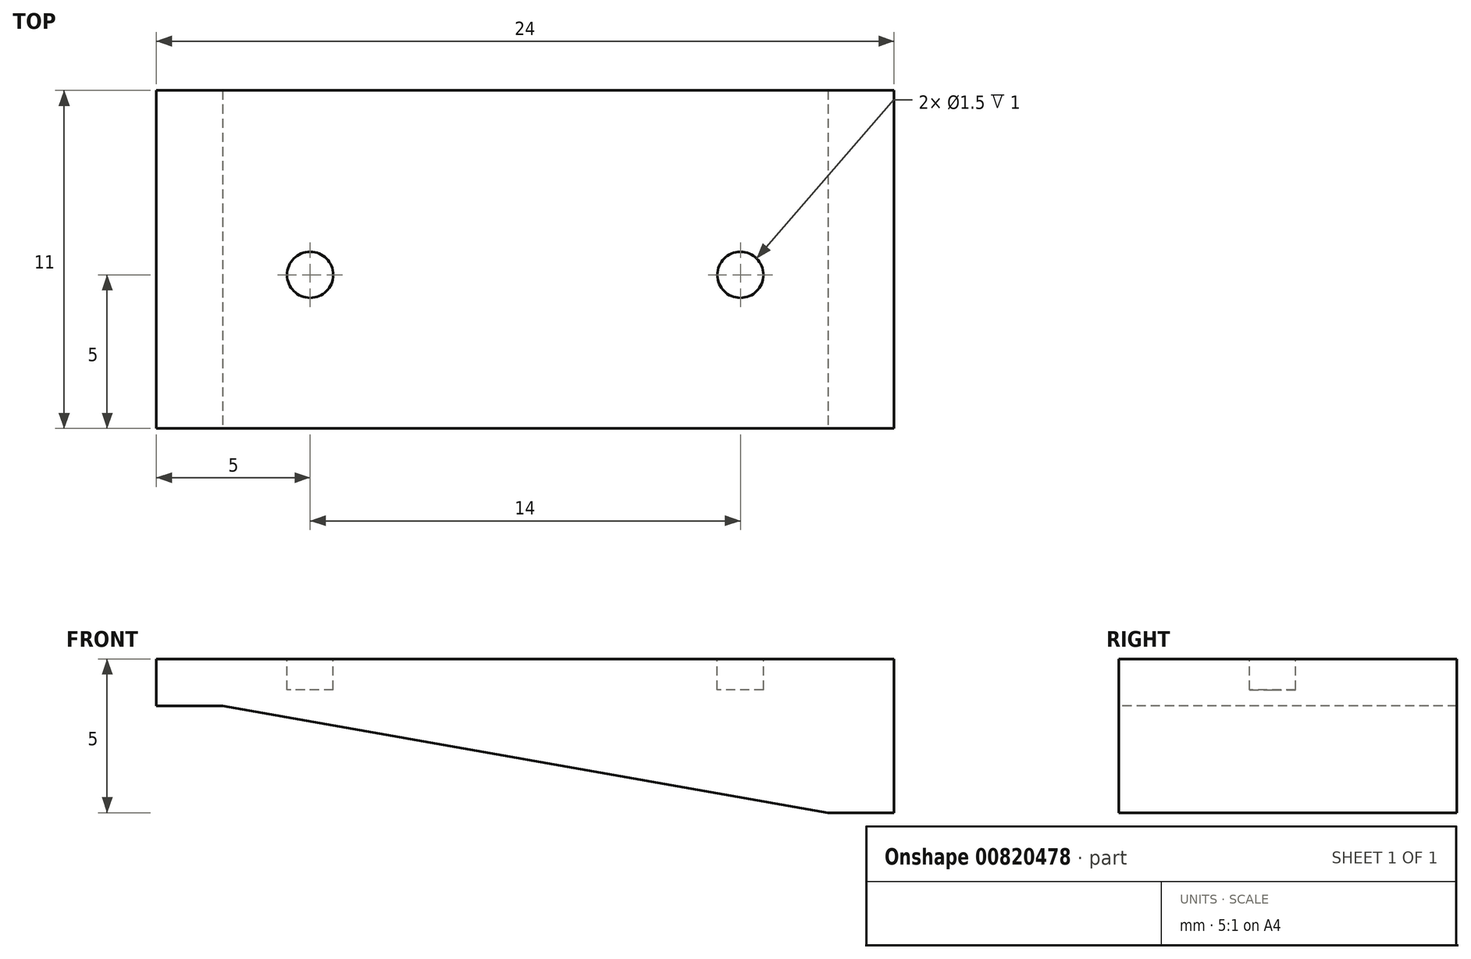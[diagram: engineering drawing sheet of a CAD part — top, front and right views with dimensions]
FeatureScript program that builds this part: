
annotation { "Feature Type Name" : "Feature", "Feature Type Description" : "" }
export const myFeature = defineFeature(function(context is Context, id is Id, definition is map)
    precondition{}
    {
        {
            var Q0;
            Q0=qCreatedBy(makeId("Top.planeOp"),FACE);
            var sketch = newSketch(context, id + "F0", { "sketchPlane" : qUnion([Q0])});
            skLineSegment(sketch, "E0.bottom", {"start": v(12, 5.5) * mm, "end": v(-12, 5.5) * mm});
            skLineSegment(sketch, "E0.top", {"start": v(12, -5.5) * mm, "end": v(-12, -5.5) * mm});
            skLineSegment(sketch, "E0.left", {"start": v(12, 5.5) * mm, "end": v(12, -5.5) * mm});
            skLineSegment(sketch, "E0.right", {"start": v(-12, 5.5) * mm, "end": v(-12, -5.5) * mm});
            skPoint(sketch, "E0.middle", {"position": v(0, 0) * mm});
            skSolve(sketch);
        }
        {
            var Q0;
            Q0=makeQuery(id+"F0.imprint","IMPRINT",FACE,{"disambiguationData":[TD([[makeQuery(id+"F0.imprint","IMPRINT",EDGE,{"derivedFrom":sQuery(id+"F0.wireOp",EDGE,"E0.bottom")}),1.0]])]});
            extrude(context, id + "F1", {"entities" : qUnion([Q0]), "depth" : 5 * mm, "offsetDistance" : 25 * mm});
        }
        {
            var Q0;
            Q0=makeQuery(id+"F1.opExtrude","CAP_FACE",FACE,{"disambiguationData":[OSD([sQuery(id+"F0.wireOp",EDGE,"E0.bottom"),sQuery(id+"F0.wireOp",EDGE,"E0.top"),sQuery(id+"F0.wireOp",EDGE,"E0.left"),sQuery(id+"F0.wireOp",EDGE,"E0.right")])],"isStart":false});
            var sketch = newSketch(context, id + "F2", { "sketchPlane" : qUnion([Q0])});
            skCircle(sketch, "E1", {"center": v(-7, -0.5) * mm, "radius": 0.75 * mm});
            skCircle(sketch, "E2", {"center": v(7, -0.5) * mm, "radius": 0.75 * mm});
            skSolve(sketch);
        }
        {
            var Q0;
            Q0=makeQuery(id+"F2.imprint","IMPRINT",FACE,{"disambiguationData":[TD([[makeQuery(id+"F2.imprint","IMPRINT",EDGE,{"derivedFrom":sQuery(id+"F2.wireOp",EDGE,"E1")}),1.0]])]});
            var Q1;
            Q1=makeQuery(id+"F2.imprint","IMPRINT",FACE,{"disambiguationData":[TD([[makeQuery(id+"F2.imprint","IMPRINT",EDGE,{"derivedFrom":sQuery(id+"F2.wireOp",EDGE,"E2")}),1.0]])]});
            extrude(context, id + "F3", {"entities" : qUnion([Q0, Q1]), "operationType" : NewBodyOperationType.REMOVE, "oppositeDirection" : true, "depth" : 1 * mm, "offsetDistance" : 25 * mm});
        }
        {
            var Q0;
            Q0=makeQuery(id+"F1.opExtrude","SWEPT_FACE",FACE,{"disambiguationData":[OSD([sQuery(id+"F0.wireOp",EDGE,"E0.top")])]});
            var sketch = newSketch(context, id + "F4", { "sketchPlane" : qUnion([Q0])});
            skLineSegment(sketch, "E3", {"start": v(9.85, 0) * mm, "end": v(-9.85, 3.47) * mm});
            skLineSegment(sketch, "E4", {"start": v(0, 0) * mm, "end": v(0, 6.77) * mm, "construction": true});
            skPoint(sketch, "E5", {"position": v(0, 1.74) * mm});
            skLineSegment(sketch, "E6", {"start": v(-9.85, 3.47) * mm, "end": v(-12, 3.47) * mm});
            skLineSegment(sketch, "E7", {"start": v(-12, 3.47) * mm, "end": v(-12, 0) * mm});
            skLineSegment(sketch, "E8", {"start": v(-12, 0) * mm, "end": v(9.85, 0) * mm});
            skSolve(sketch);
        }
        {
            var Q0;
            Q0=makeQuery(id+"F4.imprint","IMPRINT",FACE,{"disambiguationData":[TD([[makeQuery(id+"F4.imprint","IMPRINT",EDGE,{"derivedFrom":sQuery(id+"F4.wireOp",EDGE,"E3")}),1.0]])]});
            extrude(context, id + "F5", {"entities" : qUnion([Q0]), "operationType" : NewBodyOperationType.REMOVE, "endBound" : BoundingType.THROUGH_ALL, "oppositeDirection" : true, "depth" : 25 * mm, "offsetDistance" : 25 * mm});
        }
    });
